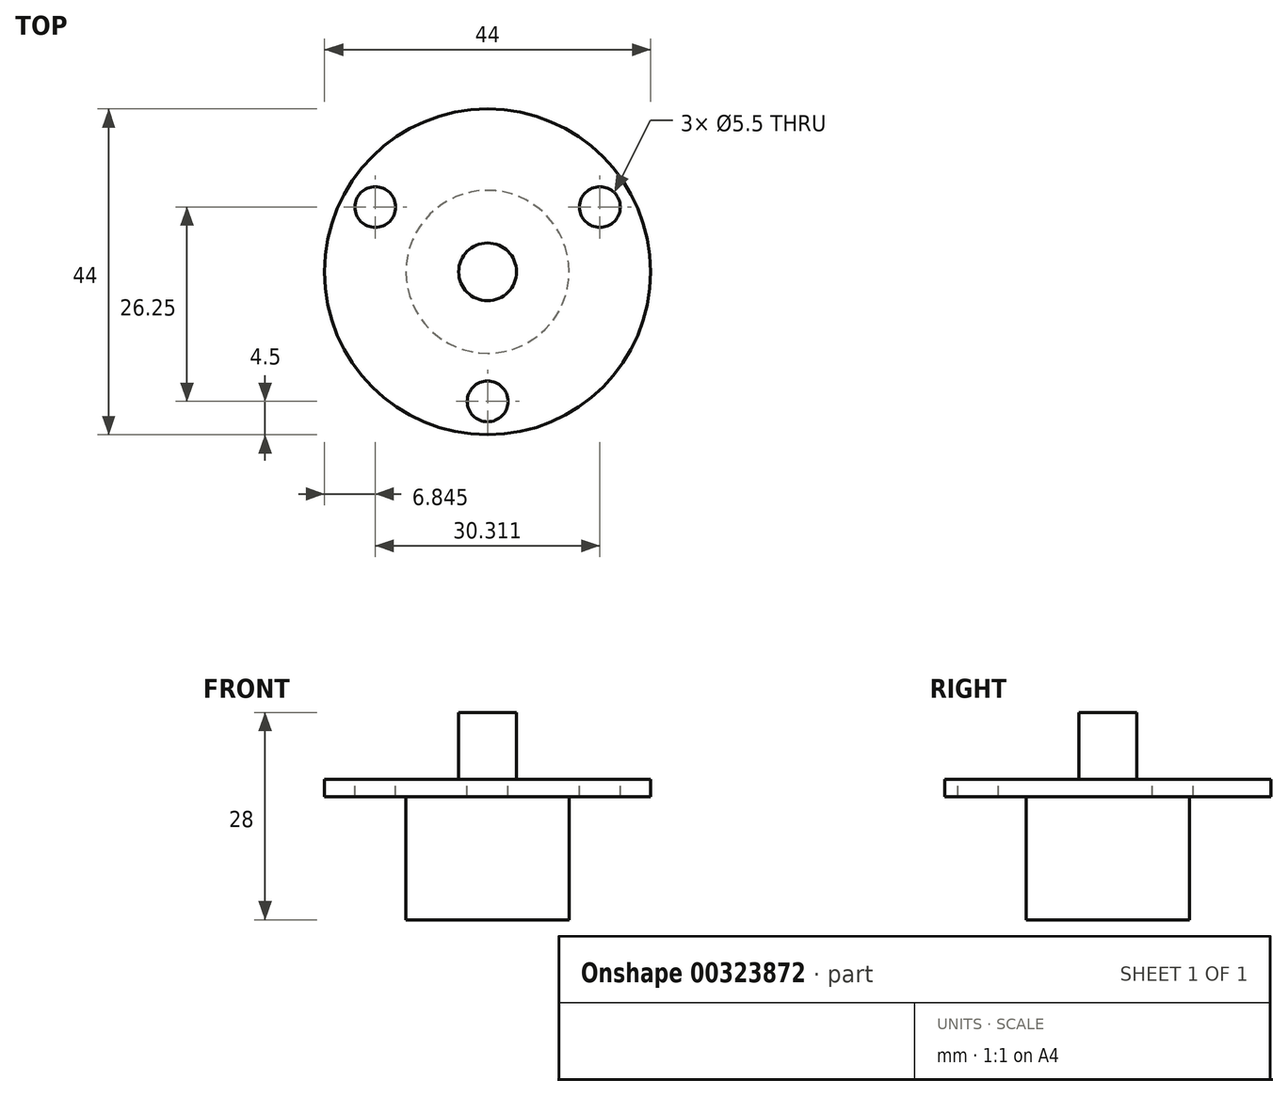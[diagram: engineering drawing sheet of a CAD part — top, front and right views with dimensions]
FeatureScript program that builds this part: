
annotation { "Feature Type Name" : "Feature", "Feature Type Description" : "" }
export const myFeature = defineFeature(function(context is Context, id is Id, definition is map)
    precondition{}
    {
        {
            var Q0;
            Q0=qCreatedBy(makeId("Top.planeOp"),FACE);
            var sketch = newSketch(context, id + "F0", { "sketchPlane" : qUnion([Q0])});
            skCircle(sketch, "E0", {"center": v(0, 0) * mm, "radius": 11 * mm});
            skSolve(sketch);
        }
        {
            var Q0;
            Q0=makeQuery(id+"F0.imprint","IMPRINT",FACE,{"disambiguationData":[TD([[makeQuery(id+"F0.imprint","IMPRINT",EDGE,{"derivedFrom":sQuery(id+"F0.wireOp",EDGE,"E0")}),1.0]])]});
            extrude(context, id + "F1", {"entities" : qUnion([Q0]), "depth" : 16.6 * mm});
        }
        {
            var Q0;
            Q0=makeQuery(id+"F1.opExtrude","CAP_FACE",FACE,{"disambiguationData":[OSD([sQuery(id+"F0.wireOp",EDGE,"E0")])],"isStart":false});
            var sketch = newSketch(context, id + "F2", { "sketchPlane" : qUnion([Q0])});
            skCircle(sketch, "E1", {"center": v(0, 0) * mm, "radius": 22 * mm});
            skSolve(sketch);
        }
        {
            var Q0;
            Q0=makeQuery(id+"F2.imprint","IMPRINT",FACE,{"disambiguationData":[TD([[makeQuery(id+"F2.imprint","IMPRINT",EDGE,{"derivedFrom":sQuery(id+"F2.wireOp",EDGE,"E1")}),1.0]])]});
            var Q1;
            Q1=makeQuery(id+"F2.imprint","IMPRINT",FACE,{"disambiguationData":[TD([[makeQuery(id+"F2.imprint","IMPRINT",EDGE,{"derivedFrom":makeQuery(id+"F1.opExtrude","CAP_EDGE",EDGE,{"disambiguationData":[OSD([sQuery(id+"F0.wireOp",EDGE,"E0")])],"isStart":false})}),1.0]])]});
            extrude(context, id + "F3", {"entities" : qUnion([Q0, Q1]), "operationType" : NewBodyOperationType.ADD, "depth" : 2.4 * mm});
        }
        {
            var Q0;
            Q0=makeQuery(id+"F3.opExtrude","CAP_FACE",FACE,{"disambiguationData":[OSD([sQuery(id+"F2.wireOp",EDGE,"E1")])],"isStart":false});
            var sketch = newSketch(context, id + "F4", { "sketchPlane" : qUnion([Q0])});
            skCircle(sketch, "E2", {"center": v(0, 0) * mm, "radius": 3.9 * mm});
            skSolve(sketch);
        }
        {
            var Q0;
            Q0=makeQuery(id+"F4.imprint","IMPRINT",FACE,{"disambiguationData":[TD([[makeQuery(id+"F4.imprint","IMPRINT",EDGE,{"derivedFrom":sQuery(id+"F4.wireOp",EDGE,"E2")}),1.0]])]});
            extrude(context, id + "F5", {"entities" : qUnion([Q0]), "operationType" : NewBodyOperationType.ADD, "depth" : 9 * mm});
        }
        {
            var Q0;
            Q0=makeQuery(id+"F3.opExtrude","CAP_FACE",FACE,{"disambiguationData":[OSD([sQuery(id+"F2.wireOp",EDGE,"E1")])],"isStart":false});
            var sketch = newSketch(context, id + "F6", { "sketchPlane" : qUnion([Q0])});
            skCircle(sketch, "E3", {"center": v(0, -17.5) * mm, "radius": 2.75 * mm});
            skCircle(sketch, "E4.1.0", {"center": v(15.16, 8.75) * mm, "radius": 2.75 * mm});
            skCircle(sketch, "E4.2.0", {"center": v(-15.16, 8.75) * mm, "radius": 2.75 * mm});
            skPoint(sketch, "E4.center", {"position": v(0, 0) * mm});
            skSolve(sketch);
        }
        {
            var Q0;
            Q0=makeQuery(id+"F6.imprint","IMPRINT",FACE,{"disambiguationData":[TD([[makeQuery(id+"F6.imprint","IMPRINT",EDGE,{"derivedFrom":sQuery(id+"F6.wireOp",EDGE,"E4.2.0")}),1.0]])]});
            var Q1;
            Q1=makeQuery(id+"F6.imprint","IMPRINT",FACE,{"disambiguationData":[TD([[makeQuery(id+"F6.imprint","IMPRINT",EDGE,{"derivedFrom":sQuery(id+"F6.wireOp",EDGE,"E4.1.0")}),1.0]])]});
            var Q2;
            Q2=makeQuery(id+"F6.imprint","IMPRINT",FACE,{"disambiguationData":[TD([[makeQuery(id+"F6.imprint","IMPRINT",EDGE,{"derivedFrom":sQuery(id+"F6.wireOp",EDGE,"E3")}),1.0]])]});
            extrude(context, id + "F7", {"entities" : qUnion([Q0, Q1, Q2]), "operationType" : NewBodyOperationType.REMOVE, "oppositeDirection" : true, "depth" : 25 * mm});
        }
    });
